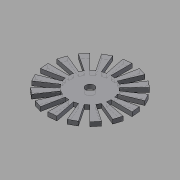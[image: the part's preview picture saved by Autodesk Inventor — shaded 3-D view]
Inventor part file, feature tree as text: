
AUTODESK INVENTOR PART (.ipt)
format: ipt  version: 2015 (Build 190159000, 159)  size: 209,408 bytes
history: native  units: mm
features: extrude x1, sketch x1
ambient origin geometry x8: Origin, YZ Plane, XZ Plane, XY Plane, X Axis, Y Axis, Z Axis, Center Point
bodies: Body1 (feature_tree)
feature tree (2):
  extrude  "Extrusion2"  Depth=1.0mm TaperAngle=0.0deg
  sketch  "Sketch1"  dims[d1=2.0mm d5=1.0mm d6=0.0mm]
